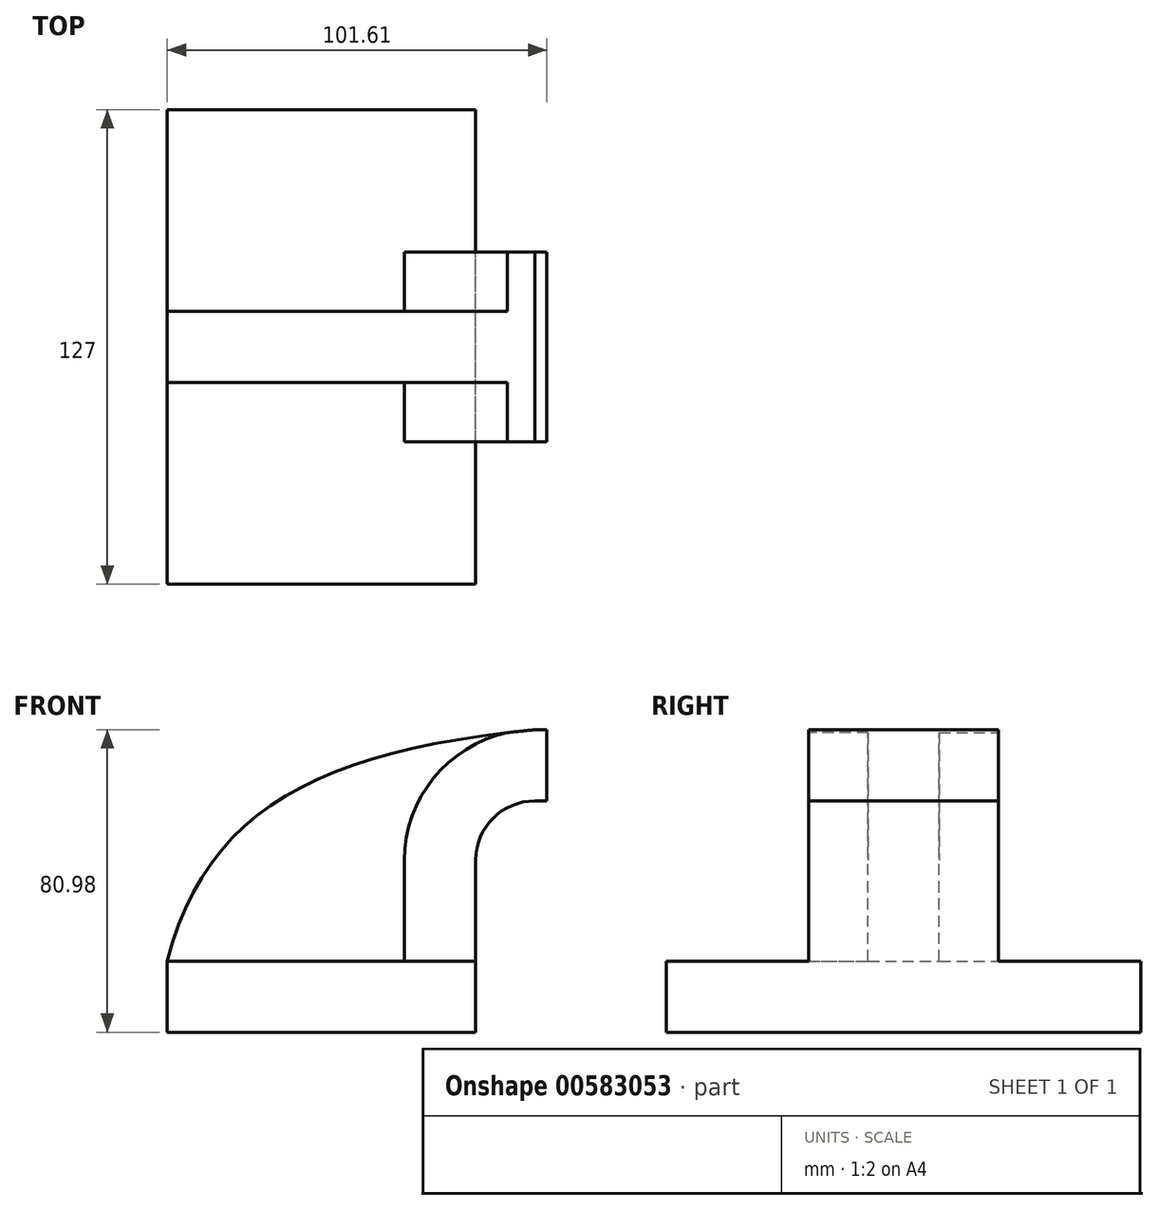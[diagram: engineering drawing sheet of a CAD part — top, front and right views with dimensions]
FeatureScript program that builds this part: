
annotation { "Feature Type Name" : "Feature", "Feature Type Description" : "" }
export const myFeature = defineFeature(function(context is Context, id is Id, definition is map)
    precondition{}
    {
        {
            var Q0;
            Q0=qCreatedBy(makeId("Front.planeOp"),FACE);
            var sketch = newSketch(context, id + "F0", { "sketchPlane" : qUnion([Q0])});
            skLineSegment(sketch, "E0.bottom", {"start": v(41.28, -9.52) * mm, "end": v(-41.27, -9.52) * mm});
            skLineSegment(sketch, "E0.top", {"start": v(41.27, 9.53) * mm, "end": v(-41.28, 9.53) * mm});
            skLineSegment(sketch, "E0.left", {"start": v(41.28, -9.52) * mm, "end": v(41.28, 9.53) * mm});
            skLineSegment(sketch, "E0.right", {"start": v(-41.27, -9.52) * mm, "end": v(-41.28, 9.53) * mm});
            skPoint(sketch, "E0.middle", {"position": v(0, 0) * mm});
            skLineSegment(sketch, "E1.bottom", {"start": v(60.33, 76.2) * mm, "end": v(111.12, 76.2) * mm});
            skLineSegment(sketch, "E1.top", {"start": v(60.33, 47.62) * mm, "end": v(111.13, 47.62) * mm});
            skLineSegment(sketch, "E1.left", {"start": v(60.33, 76.2) * mm, "end": v(60.33, 47.62) * mm});
            skLineSegment(sketch, "E1.right", {"start": v(111.13, 76.2) * mm, "end": v(111.13, 47.62) * mm});
            skLineSegment(sketch, "E2", {"start": v(41.27, 9.53) * mm, "end": v(41.27, 36.53) * mm});
            skArc(sketch, "E3", {"start": v(41.27, 36.53) * mm, "mid": v(45.92, 47.75) * mm, "end": v(57.15, 52.4) * mm});
            skLineSegment(sketch, "E4", {"start": v(57.15, 52.4) * mm, "end": v(85.73, 52.4) * mm});
            skPoint(sketch, "E4.endSnap0", {"position": v(85.73, 47.62) * mm});
            skLineSegment(sketch, "E5.0", {"start": v(57.15, 71.45) * mm, "end": v(85.73, 71.45) * mm});
            skArc(sketch, "E5.1", {"start": v(22.23, 36.53) * mm, "mid": v(32.45, 61.22) * mm, "end": v(57.15, 71.45) * mm});
            skLineSegment(sketch, "E5.2", {"start": v(22.23, 9.53) * mm, "end": v(22.23, 36.53) * mm});
            skLineSegment(sketch, "E6", {"start": v(85.72, 47.62) * mm, "end": v(85.72, 76.2) * mm});
            skFitSpline(sketch, "E7", {"points": [v(-41.28, 9.53) * mm, v(57.15, 71.45) * mm], "startDerivative": vector(31.37, 122.5) * mm, "endDerivative": vector(171.45, 16.65) * mm});
            skSolve(sketch);
        }
        {
            var Q0;
            Q0=makeQuery(id+"F0.imprint","IMPRINT",FACE,{"disambiguationData":[TD([[makeQuery(id+"F0.imprint","IMPRINT",EDGE,{"derivedFrom":sQuery(id+"F0.wireOp",EDGE,"E0.bottom")}),-1.0]])]});
            extrude(context, id + "F1", {"entities" : qUnion([Q0]), "endBound" : BoundingType.SYMMETRIC, "depth" : 127 * mm, "offsetDistance" : 25.4 * mm});
        }
        {
            var Q0;
            {var subQ1=sQuery(id+"F0.wireOp",EDGE,"E2");Q0=makeQuery(id+"F0.imprint","IMPRINT",FACE,{"disambiguationData":[TD([[makeQuery(id+"F0.imprint","IMPRINT",EDGE,{"derivedFrom":subQ1}),1.0]])]});}
            extrude(context, id + "F2", {"entities" : qUnion([Q0]), "operationType" : NewBodyOperationType.ADD, "endBound" : BoundingType.SYMMETRIC, "depth" : 50.8 * mm, "offsetDistance" : 25.4 * mm});
        }
        {
            var Q0;
            {var subQ3=sQuery(id+"F0.wireOp",EDGE,"E5.2");Q0=makeQuery(id+"F0.imprint","IMPRINT",FACE,{"disambiguationData":[TD([[makeQuery(id+"F0.imprint","IMPRINT",EDGE,{"derivedFrom":subQ3}),1.0]])]});}
            extrude(context, id + "F3", {"entities" : qUnion([Q0]), "operationType" : NewBodyOperationType.ADD, "endBound" : BoundingType.SYMMETRIC, "depth" : 19.05 * mm, "offsetDistance" : 25.4 * mm});
        }
    });
